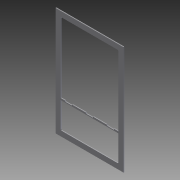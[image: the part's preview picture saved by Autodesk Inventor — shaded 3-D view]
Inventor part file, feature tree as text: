
AUTODESK INVENTOR PART (.ipt)
format: ipt  version: 2011 (Build 150239000, 239)  size: 1,053,184 bytes
history: native  units: in
note: dims shown in document units (in); Inventor stores cm internally (conversion verified against a paired STEP export)
features: extrude x28, sketch x28, fillet x4
ambient origin geometry x8: Origin, YZ Plane, XZ Plane, XY Plane, X Axis, Y Axis, Z Axis, Center Point
bodies: Solid1 (feature_tree)
feature tree (60):
  extrude  "Extrusion1"  Depth=35.0in
  extrude  "Extrusion2"  Depth=1.5in
  extrude  "Extrusion3"  Depth=0.75in
  extrude  "Extrusion4"  Depth=2.25in
  fillet  "Fillet1"  Radius=0.156in
  extrude  "Extrusion5"  Depth=0.25in TaperAngle=0.0deg
  extrude  "Extrusion6"  Depth=3.0in
  extrude  "Extrusion7"  Depth=1.0in
  extrude  "Extrusion8"  Depth=0.25in TaperAngle=0.0deg
  extrude  "Extrusion9"  Depth=3.5in
  extrude  "Extrusion10"  Depth=3.5in
  extrude  "Extrusion11"  Depth=0.25in TaperAngle=0.0deg
  extrude  "Extrusion12"  Depth=0.25in
  extrude  "Extrusion13"  Depth=1.0in
  extrude  "Extrusion14"  Depth=1.0in
  extrude  "Extrusion15"  Depth=1.0in
  extrude  "Extrusion16"  Depth=1.0in
  extrude  "Extrusion17"  Depth=1.0in
  extrude  "Extrusion18"  Depth=1.0in
  extrude  "Extrusion19"  Depth=1.0in
  extrude  "Extrusion20"  Depth=1.0in
  extrude  "Extrusion21"  Depth=1.0in
  fillet  "Fillet2"  Radius=1.0in
  extrude  "Extrusion22"  Depth=0.25in TaperAngle=0.0deg
  extrude  "Extrusion23"  Depth=2.0in
  extrude  "Extrusion24"  Depth=2.0in
  extrude  "Extrusion25"  Depth=2.0in
  extrude  "Extrusion26"  Depth=2.0in
  fillet  "Fillet3"  Radius=2.0in
  extrude  "Extrusion27"  Depth=2.0in
  extrude  "Extrusion28"  Depth=2.0in
  fillet  "Fillet4"  Radius=2.0in
  sketch  "Sketch1"  dims[d0=19.5in d1=35.0in]
  sketch  "Sketch2"  dims[d2=0.25in d3=0.0in d4=1.5in]
  sketch  "Sketch3"  dims[d5=3.0in d6=0.75in]
  sketch  "Sketch4"  dims[d7=0.75in d8=2.25in d9=0.156in]
  sketch  "Sketch5"  dims[d10=0.156in d11=0.25in d12=0.0in]
  sketch  "Sketch6"  dims[d13=1.5in d14=3.0in]
  sketch  "Sketch7"  dims[d15=1.5in d16=1.0in]
  sketch  "Sketch8"  dims[d17=32.25in d18=0.25in d19=0.0in]
  sketch  "Sketch9"  dims[d20=2.0in d21=3.5in]
  sketch  "Sketch10"  dims[d22=2.0in d23=3.5in]
  sketch  "Sketch11"  dims[d24=1.5in d25=0.25in d26=0.0in]
  sketch  "Sketch12"  dims[d27=0.25in d28=0.25in]
  sketch  "Sketch13"  dims[d29=0.25in d30=1.0in]
  sketch  "Sketch14"  dims[d31=1.0in d32=1.0in]
  sketch  "Sketch15"  dims[d33=1.0in d34=1.0in]
  sketch  "Sketch16"  dims[d35=1.0in d36=1.0in]
  sketch  "Sketch17"  dims[d37=1.0in d38=1.0in]
  sketch  "Sketch18"  dims[d39=1.0in d40=1.0in]
  sketch  "Sketch19"  dims[d41=1.0in d42=1.0in]
  sketch  "Sketch20"  dims[d43=1.0in d44=1.0in]
  sketch  "Sketch21"  dims[d45=1.0in d46=1.0in d47=1.0in]
  sketch  "Sketch22"  dims[d48=1.0in d49=0.25in d50=0.0in]
  sketch  "Sketch23"  dims[d51=2.0in d52=2.0in]
  sketch  "Sketch24"  dims[d53=2.0in d54=2.0in]
  sketch  "Sketch25"  dims[d55=2.0in d56=2.0in]
  sketch  "Sketch26"  dims[d57=2.0in d58=2.0in d59=2.0in]
  sketch  "Sketch27"  dims[d60=2.0in d61=2.0in]
  sketch  "Sketch28"  dims[d62=2.0in d63=2.0in d64=2.0in d65=2.0in d66=2.0in d67=2.0in d68=0.25in d69=0.0in d70=0.25in d71=0.0in d72=0.25in d73=0.0in d74=0.75in d75=0.25in d76=0.75in d77=0.25in d78=2.0in d79=2.0in d80=2.0in d81=2.0in d82=2.0in d83=2.0in d84=2.0in d85=2.0in d86=0.25in d87=0.0in d88=2.0in d89=2.0in d90=2.0in d91=2.0in d92=0.25in d93=0.0in d94=2.0in d95=2.0in d96=0.25in d97=0.0in d98=0.25in d99=0.25in d100=0.0in d101=9.0in d102=0.5in d103=0.75in d104=1.0in d105=0.0in d106=1.0in d107=0.0in d108=9.25in d109=0.25in d110=2.0in d111=0.25in d112=2.0in d113=4.0in d114=2.0in d115=1.0in d116=0.0in d117=0.25in d118=0.0in d119=0.5in d120=2.5in d121=0.5in d122=2.5in d123=0.156in d124=0.156in d125=0.25in d126=0.0in d127=1.0in d128=0.0in d129=1.0in d130=0.0in d131=0.25in d132=0.0in d133=0.25in d134=0.0in d135=0.25in d136=8.25in d137=1.0in d138=2.0in d139=0.25in d140=4.0in d141=2.0in d142=4.0in d143=2.0in d144=0.25in d145=0.0in d146=0.25in d147=0.0in d148=0.25in d149=0.0in d150=3.86in d151=1.0in d152=0.0in d153=0.25in d154=1.5in d155=0.25in d156=0.0in d157=0.25in d158=0.25in d159=0.0in d160=0.25in d161=0.25in d162=0.0in d163=0.25in]
